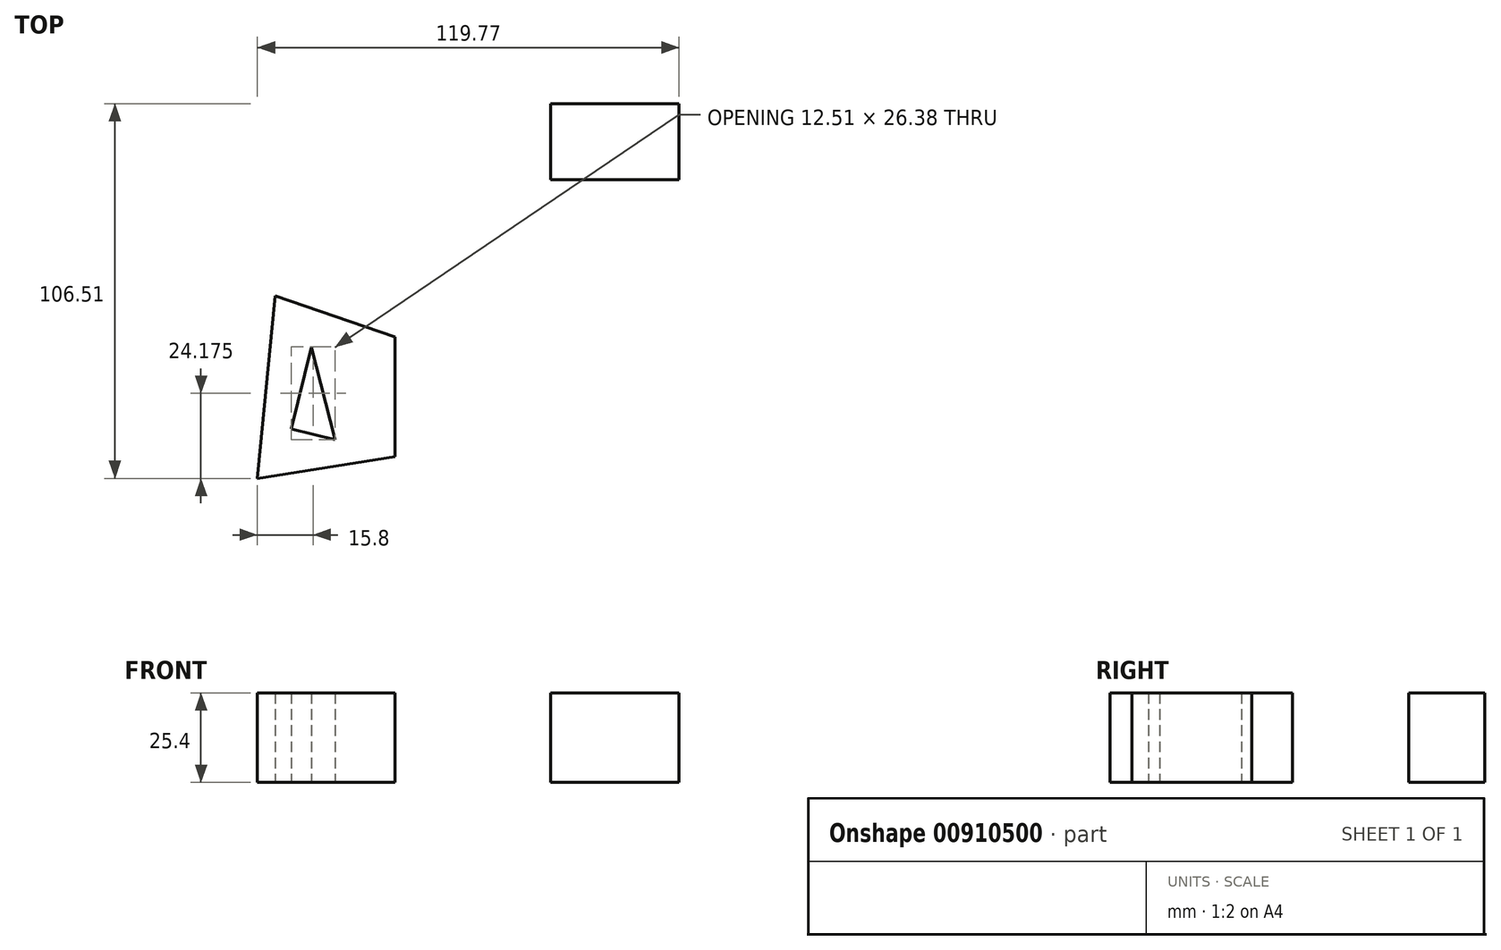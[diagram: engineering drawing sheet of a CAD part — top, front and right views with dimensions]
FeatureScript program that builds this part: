
annotation { "Feature Type Name" : "Feature", "Feature Type Description" : "" }
export const myFeature = defineFeature(function(context is Context, id is Id, definition is map)
    precondition{}
    {
        {
            var Q0;
            Q0=qCreatedBy(makeId("Top.planeOp"),FACE);
            var sketch = newSketch(context, id + "F0", { "sketchPlane" : qUnion([Q0])});
            skCircle(sketch, "E0", {"center": v(-62.28, 52.52) * mm, "radius": 11.18 * mm});
            skLineSegment(sketch, "E1.bottom", {"start": v(23.25, 37.16) * mm, "end": v(59.79, 37.16) * mm});
            skLineSegment(sketch, "E1.top", {"start": v(23.25, 15.57) * mm, "end": v(59.79, 15.57) * mm});
            skLineSegment(sketch, "E1.left", {"start": v(23.25, 37.16) * mm, "end": v(23.25, 15.57) * mm});
            skLineSegment(sketch, "E1.right", {"start": v(59.79, 37.16) * mm, "end": v(59.79, 15.57) * mm});
            skLineSegment(sketch, "E2", {"start": v(-55, -17.45) * mm, "end": v(-20.95, -29.08) * mm});
            skLineSegment(sketch, "E3", {"start": v(-20.95, -29.08) * mm, "end": v(-20.95, -63.13) * mm});
            skLineSegment(sketch, "E4", {"start": v(-20.95, -63.13) * mm, "end": v(-59.98, -69.35) * mm});
            skLineSegment(sketch, "E5", {"start": v(-59.98, -69.35) * mm, "end": v(-55, -17.45) * mm});
            skLineSegment(sketch, "E6", {"start": v(-44.62, -31.99) * mm, "end": v(-50.43, -55.24) * mm});
            skLineSegment(sketch, "E7", {"start": v(-50.43, -55.24) * mm, "end": v(-37.93, -58.36) * mm});
            skLineSegment(sketch, "E8", {"start": v(-37.93, -58.36) * mm, "end": v(-44.62, -31.99) * mm});
            skLineSegment(sketch, "E9", {"start": v(-82.91, 71.7) * mm, "end": v(-82.91, 30.26) * mm, "construction": true});
            skSolve(sketch);
        }
        {
            var Q0;
            Q0=makeQuery(id+"F0.imprint","IMPRINT",FACE,{"disambiguationData":[TD([[makeQuery(id+"F0.imprint","IMPRINT",EDGE,{"derivedFrom":sQuery(id+"F0.wireOp",EDGE,"E2")}),-1.0]])]});
            extrude(context, id + "F1", {"entities" : qUnion([Q0]), "depth" : 25.4 * mm, "offsetDistance" : 25.4 * mm});
        }
        {
            var Q0;
            Q0=makeQuery(id+"F0.imprint","IMPRINT",FACE,{"disambiguationData":[TD([[makeQuery(id+"F0.imprint","IMPRINT",EDGE,{"derivedFrom":sQuery(id+"F0.wireOp",EDGE,"E1.bottom")}),-1.0]])]});
            extrude(context, id + "F2", {"entities" : qUnion([Q0]), "depth" : 25.4 * mm, "offsetDistance" : 25.4 * mm});
        }
        {
            var Q0;
            Q0=sQuery(id+"F0.wireOp",EDGE,"E0");
            extrude(context, id + "F3", {"bodyType" : ToolBodyType.SURFACE, "surfaceEntities" : qUnion([Q0]), "depth" : 25.4 * mm, "offsetDistance" : 25.4 * mm});
        }
    });
